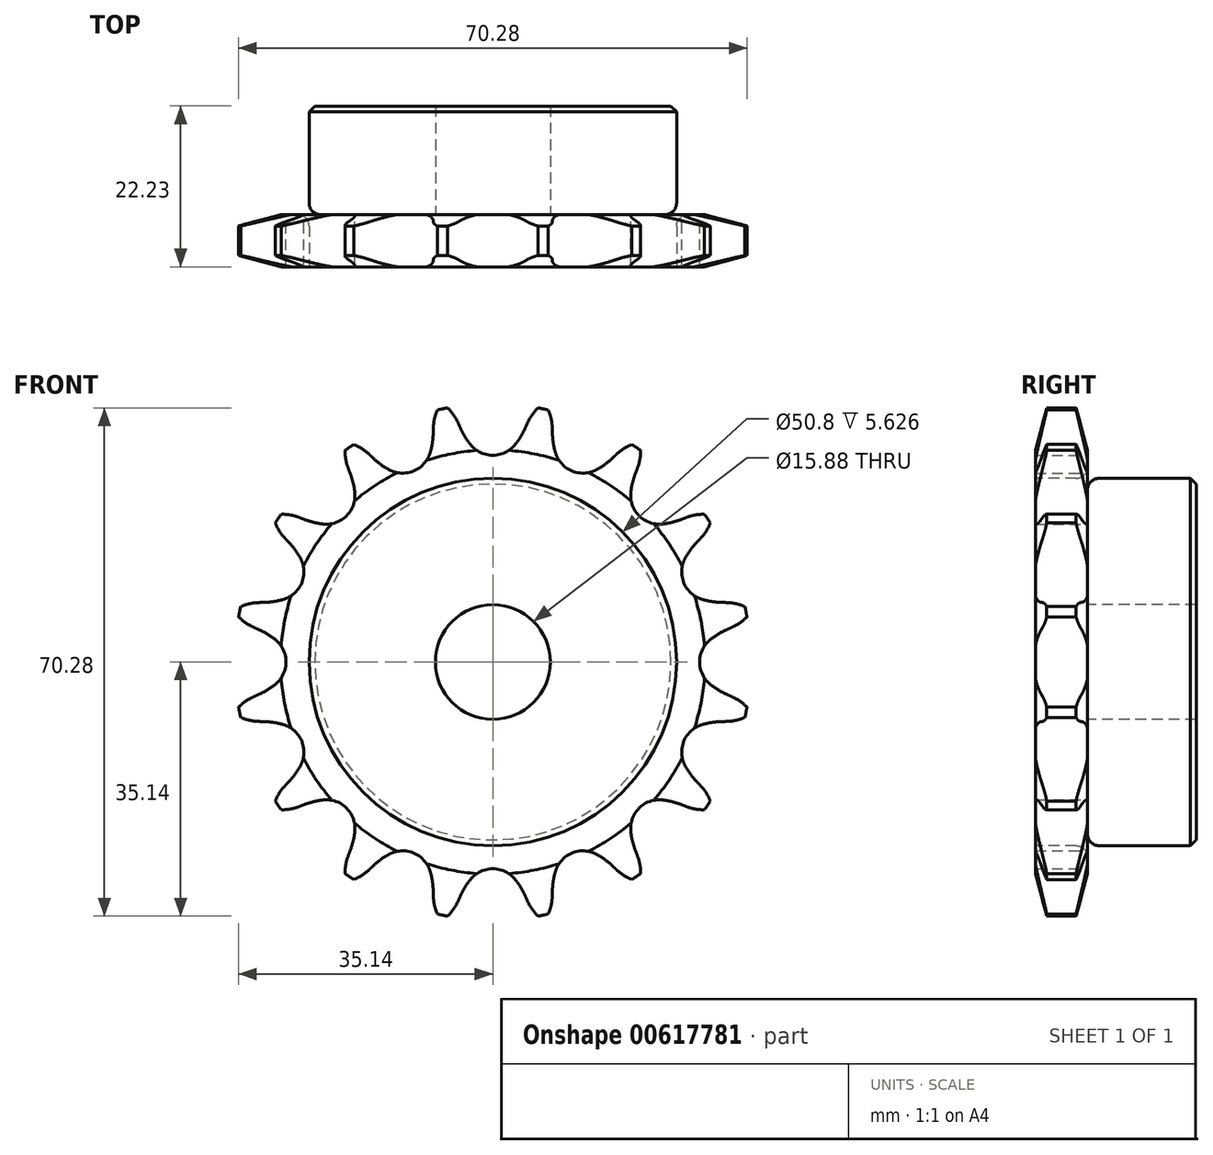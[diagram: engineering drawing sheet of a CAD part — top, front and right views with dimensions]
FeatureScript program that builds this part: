
annotation { "Feature Type Name" : "Feature", "Feature Type Description" : "" }
export const myFeature = defineFeature(function(context is Context, id is Id, definition is map)
    precondition{}
    {
        {
            var Q0;
            Q0=qCreatedBy(makeId("Right.planeOp"),FACE);
            var sketch = newSketch(context, id + "F0", { "sketchPlane" : qUnion([Q0])});
            skLineSegment(sketch, "E0", {"start": v(0, 0) * mm, "end": v(15.45, 0) * mm, "construction": true});
            skLineSegment(sketch, "E1.bottom", {"start": v(0, 7.94) * mm, "end": v(7.21, 7.94) * mm});
            skLineSegment(sketch, "E1.top", {"start": v(0, 35.69) * mm, "end": v(7.21, 35.69) * mm});
            skLineSegment(sketch, "E1.left", {"start": v(0, 7.94) * mm, "end": v(0, 35.69) * mm});
            skLineSegment(sketch, "E1.right", {"start": v(7.21, 7.94) * mm, "end": v(7.21, 35.69) * mm});
            skLineSegment(sketch, "E2.bottom", {"start": v(0, 7.94) * mm, "end": v(22.23, 7.94) * mm});
            skLineSegment(sketch, "E2.top", {"start": v(0, 25.4) * mm, "end": v(22.23, 25.4) * mm});
            skLineSegment(sketch, "E2.left", {"start": v(0, 7.94) * mm, "end": v(0, 25.4) * mm});
            skLineSegment(sketch, "E2.right", {"start": v(22.23, 7.94) * mm, "end": v(22.23, 25.4) * mm});
            skLineSegment(sketch, "E3.MirrorCS", {"start": v(0, -7.94) * mm, "end": v(7.21, -7.94) * mm});
            skLineSegment(sketch, "E4.MirrorCS", {"start": v(22.23, -7.94) * mm, "end": v(22.23, -25.4) * mm});
            skLineSegment(sketch, "E5.MirrorCS", {"start": v(0, -7.94) * mm, "end": v(0, -25.4) * mm});
            skLineSegment(sketch, "E6.MirrorCS", {"start": v(0, -35.69) * mm, "end": v(7.21, -35.69) * mm});
            skLineSegment(sketch, "E7.MirrorCS", {"start": v(0, -7.94) * mm, "end": v(0, -35.69) * mm});
            skLineSegment(sketch, "E8.MirrorCS", {"start": v(7.21, -7.94) * mm, "end": v(7.21, -35.69) * mm});
            skLineSegment(sketch, "E9.MirrorCS", {"start": v(0, -7.94) * mm, "end": v(22.23, -7.94) * mm});
            skLineSegment(sketch, "E10.MirrorCS", {"start": v(0, -25.4) * mm, "end": v(22.23, -25.4) * mm});
            skSolve(sketch);
        }
        {
            var Q0;
            {var subQ0=sQuery(id+"F0.wireOp",EDGE,"E1.top");Q0=makeQuery(id+"F0.imprint","IMPRINT",FACE,{"disambiguationData":[TD([[makeQuery(id+"F0.imprint","IMPRINT",EDGE,{"derivedFrom":subQ0}),-1.0]])]});}
            var Q1;
            {var subQ5=sQuery(id+"F0.wireOp",EDGE,"E2.left");Q1=makeQuery(id+"F0.imprint","IMPRINT",FACE,{"disambiguationData":[TD([[makeQuery(id+"F0.imprint","IMPRINT",EDGE,{"derivedFrom":subQ5}),-1.0]])]});}
            var Q2;
            {var subQ5=sQuery(id+"F0.wireOp",EDGE,"E2.right");Q2=makeQuery(id+"F0.imprint","IMPRINT",FACE,{"disambiguationData":[TD([[makeQuery(id+"F0.imprint","IMPRINT",EDGE,{"derivedFrom":subQ5}),1.0]])]});}
            var Q3;
            Q3=sQuery(id+"F0.wireOp",EDGE,"E0");
            revolve(context, id + "F1", {"entities" : qUnion([Q0, Q1, Q2]), "axis" : qUnion([Q3]), "revolveType" : RevolveType.FULL});
        }
        {
            var Q0;
            Q0=makeQuery(id+"F1.opRevolve","SWEPT_EDGE",EDGE,{"disambiguationData":[OSD([sQuery(id+"F0.wireOp",EDGE,"E1.right"),sQuery(id+"F0.wireOp",EDGE,"E2.top")])]});
            fillet(context, id + "F2", {"entities" : qUnion([Q0]), "radius" : 1.59 * mm, "tangentPropagation" : true, "allowEdgeOverflow" : false});
        }
        {
            var Q0;
            Q0=makeQuery(id+"F1.opRevolve","SWEPT_EDGE",EDGE,{"disambiguationData":[OSD([sQuery(id+"F0.wireOp",EDGE,"E2.top"),sQuery(id+"F0.wireOp",EDGE,"E2.right")])]});
            chamfer(context, id + "F3", {"entities" : qUnion([Q0]), "width" : 0.8 * mm, "tangentPropagation" : true});
        }
        {
            var Q0;
            Q0=makeQuery(id+"F1.opRevolve","SWEPT_EDGE",EDGE,{"disambiguationData":[OSD([sQuery(id+"F0.wireOp",EDGE,"E1.top"),sQuery(id+"F0.wireOp",EDGE,"E1.left")])]});
            var Q1;
            Q1=makeQuery(id+"F1.opRevolve","SWEPT_EDGE",EDGE,{"disambiguationData":[OSD([sQuery(id+"F0.wireOp",EDGE,"E1.top"),sQuery(id+"F0.wireOp",EDGE,"E1.right")])]});
            chamfer(context, id + "F4", {"entities" : qUnion([Q0, Q1]), "chamferType" : ChamferType.TWO_OFFSETS, "width1" : 6.35 * mm, "oppositeDirection" : false, "width2" : 1.57 * mm, "tangentPropagation" : true});
        }
        {
            var Q0;
            Q0=makeQuery(id+"F1.opRevolve","SWEPT_FACE",FACE,{"disambiguationData":[OSD([sQuery(id+"F0.wireOp",EDGE,"E1.left"),sQuery(id+"F0.wireOp",EDGE,"E2.left")])]});
            var sketch = newSketch(context, id + "F5", { "sketchPlane" : qUnion([Q0])});
            skCircle(sketch, "E11", {"center": v(0, 0) * mm, "radius": 32.55 * mm, "construction": true});
            skLineSegment(sketch, "E12", {"start": v(0, 0) * mm, "end": v(0, 32.55) * mm, "construction": true});
            skLineSegment(sketch, "E13", {"start": v(0, 32.55) * mm, "end": v(44.62, 32.55) * mm, "construction": true});
            skLineSegment(sketch, "E14", {"start": v(0, 32.55) * mm, "end": v(5, 36.56) * mm, "construction": true});
            skLineSegment(sketch, "E15", {"start": v(5, 36.56) * mm, "end": v(-4.46, 32.3) * mm, "construction": true});
            skLineSegment(sketch, "E16", {"start": v(-4.46, 32.3) * mm, "end": v(-4.82, 33.1) * mm});
            skLineSegment(sketch, "E17", {"start": v(0, 0) * mm, "end": v(-7.13, 35.85) * mm});
            skArc(sketch, "E18", {"start": v(-7.13, 35.85) * mm, "mid": v(-15.87, 26.15) * mm, "end": v(-4.82, 33.1) * mm, "construction": true});
            skArc(sketch, "E19", {"start": v(-4.82, 33.1) * mm, "mid": v(-5.78, 34.63) * mm, "end": v(-7.13, 35.85) * mm});
            skLineSegment(sketch, "E20", {"start": v(-4.82, 33.1) * mm, "end": v(-4.82, 33.1) * mm});
            skLineSegment(sketch, "E21", {"start": v(0.5, 21.28) * mm, "end": v(0.38, 21.56) * mm, "construction": true});
            skArc(sketch, "E22", {"start": v(-4.46, 32.3) * mm, "mid": v(-3.84, 31.14) * mm, "end": v(-3.1, 30.07) * mm});
            skArc(sketch, "E23", {"start": v(-3.1, 30.07) * mm, "mid": v(13.83, 41.97) * mm, "end": v(-4.46, 32.3) * mm, "construction": true});
            skArc(sketch, "E24.MirrorCS", {"start": v(4.82, 33.1) * mm, "mid": v(5.78, 34.63) * mm, "end": v(7.13, 35.85) * mm});
            skLineSegment(sketch, "E25.MirrorCS", {"start": v(4.46, 32.3) * mm, "end": v(4.82, 33.1) * mm});
            skArc(sketch, "E26.MirrorCS", {"start": v(4.46, 32.3) * mm, "mid": v(3.84, 31.14) * mm, "end": v(3.1, 30.07) * mm});
            skArc(sketch, "E27", {"start": v(3.1, 30.07) * mm, "mid": v(0, 36.51) * mm, "end": v(-3.1, 30.07) * mm, "construction": true});
            skArc(sketch, "E28", {"start": v(-3.1, 30.07) * mm, "mid": v(0, 28.59) * mm, "end": v(3.1, 30.07) * mm});
            skArc(sketch, "E29.1.0", {"start": v(-17.12, 28.74) * mm, "mid": v(-18.6, 29.79) * mm, "end": v(-20.3, 30.4) * mm});
            skLineSegment(sketch, "E29.1.1", {"start": v(-16.48, 28.14) * mm, "end": v(-17.12, 28.74) * mm});
            skArc(sketch, "E29.1.2", {"start": v(-16.48, 28.14) * mm, "mid": v(-15.47, 27.3) * mm, "end": v(-14.36, 26.6) * mm});
            skArc(sketch, "E29.1.3", {"start": v(-14.36, 26.6) * mm, "mid": v(-10.94, 26.41) * mm, "end": v(-8.65, 28.96) * mm});
            skArc(sketch, "E29.1.4", {"start": v(-8.24, 31.55) * mm, "mid": v(-8.37, 30.24) * mm, "end": v(-8.65, 28.96) * mm});
            skLineSegment(sketch, "E29.1.5", {"start": v(-8.24, 31.55) * mm, "end": v(-8.22, 32.42) * mm});
            skArc(sketch, "E29.1.6", {"start": v(-8.22, 32.42) * mm, "mid": v(-7.91, 34.21) * mm, "end": v(-7.13, 35.85) * mm});
            skArc(sketch, "E29.2.0", {"start": v(-26.8, 20) * mm, "mid": v(-28.58, 20.4) * mm, "end": v(-30.4, 20.3) * mm});
            skLineSegment(sketch, "E29.2.1", {"start": v(-26, 19.69) * mm, "end": v(-26.8, 20) * mm});
            skArc(sketch, "E29.2.2", {"start": v(-26, 19.69) * mm, "mid": v(-24.74, 19.3) * mm, "end": v(-23.45, 19.08) * mm});
            skArc(sketch, "E29.2.3", {"start": v(-23.45, 19.08) * mm, "mid": v(-20.21, 20.21) * mm, "end": v(-19.08, 23.45) * mm});
            skArc(sketch, "E29.2.4", {"start": v(-19.69, 26) * mm, "mid": v(-19.3, 24.74) * mm, "end": v(-19.08, 23.45) * mm});
            skLineSegment(sketch, "E29.2.5", {"start": v(-19.69, 26) * mm, "end": v(-20, 26.8) * mm});
            skArc(sketch, "E29.2.6", {"start": v(-20, 26.8) * mm, "mid": v(-20.4, 28.58) * mm, "end": v(-20.3, 30.4) * mm});
            skArc(sketch, "E29.3.0", {"start": v(-32.42, 8.22) * mm, "mid": v(-34.21, 7.91) * mm, "end": v(-35.85, 7.13) * mm});
            skLineSegment(sketch, "E29.3.1", {"start": v(-31.55, 8.24) * mm, "end": v(-32.42, 8.22) * mm});
            skArc(sketch, "E29.3.2", {"start": v(-31.55, 8.24) * mm, "mid": v(-30.24, 8.37) * mm, "end": v(-28.96, 8.65) * mm});
            skArc(sketch, "E29.3.3", {"start": v(-28.96, 8.65) * mm, "mid": v(-26.41, 10.94) * mm, "end": v(-26.6, 14.36) * mm});
            skArc(sketch, "E29.3.4", {"start": v(-28.14, 16.48) * mm, "mid": v(-27.3, 15.47) * mm, "end": v(-26.6, 14.36) * mm});
            skLineSegment(sketch, "E29.3.5", {"start": v(-28.14, 16.48) * mm, "end": v(-28.74, 17.12) * mm});
            skArc(sketch, "E29.3.6", {"start": v(-28.74, 17.12) * mm, "mid": v(-29.79, 18.6) * mm, "end": v(-30.4, 20.3) * mm});
            skArc(sketch, "E29.4.0", {"start": v(-33.1, -4.82) * mm, "mid": v(-34.63, -5.78) * mm, "end": v(-35.85, -7.13) * mm});
            skLineSegment(sketch, "E29.4.1", {"start": v(-32.3, -4.46) * mm, "end": v(-33.1, -4.82) * mm});
            skArc(sketch, "E29.4.2", {"start": v(-32.3, -4.46) * mm, "mid": v(-31.14, -3.84) * mm, "end": v(-30.07, -3.1) * mm});
            skArc(sketch, "E29.4.3", {"start": v(-30.07, -3.1) * mm, "mid": v(-28.59, 0) * mm, "end": v(-30.07, 3.1) * mm});
            skArc(sketch, "E29.4.4", {"start": v(-32.3, 4.46) * mm, "mid": v(-31.14, 3.84) * mm, "end": v(-30.07, 3.1) * mm});
            skLineSegment(sketch, "E29.4.5", {"start": v(-32.3, 4.46) * mm, "end": v(-33.1, 4.82) * mm});
            skArc(sketch, "E29.4.6", {"start": v(-33.1, 4.82) * mm, "mid": v(-34.63, 5.78) * mm, "end": v(-35.85, 7.13) * mm});
            skArc(sketch, "E29.5.0", {"start": v(-28.74, -17.12) * mm, "mid": v(-29.79, -18.6) * mm, "end": v(-30.4, -20.3) * mm});
            skLineSegment(sketch, "E29.5.1", {"start": v(-28.14, -16.48) * mm, "end": v(-28.74, -17.12) * mm});
            skArc(sketch, "E29.5.2", {"start": v(-28.14, -16.48) * mm, "mid": v(-27.3, -15.47) * mm, "end": v(-26.6, -14.36) * mm});
            skArc(sketch, "E29.5.3", {"start": v(-26.6, -14.36) * mm, "mid": v(-26.41, -10.94) * mm, "end": v(-28.96, -8.65) * mm});
            skArc(sketch, "E29.5.4", {"start": v(-31.55, -8.24) * mm, "mid": v(-30.24, -8.37) * mm, "end": v(-28.96, -8.65) * mm});
            skLineSegment(sketch, "E29.5.5", {"start": v(-31.55, -8.24) * mm, "end": v(-32.42, -8.22) * mm});
            skArc(sketch, "E29.5.6", {"start": v(-32.42, -8.22) * mm, "mid": v(-34.21, -7.91) * mm, "end": v(-35.85, -7.13) * mm});
            skArc(sketch, "E29.6.0", {"start": v(-20, -26.8) * mm, "mid": v(-20.4, -28.58) * mm, "end": v(-20.3, -30.4) * mm});
            skLineSegment(sketch, "E29.6.1", {"start": v(-19.69, -26) * mm, "end": v(-20, -26.8) * mm});
            skArc(sketch, "E29.6.2", {"start": v(-19.69, -26) * mm, "mid": v(-19.3, -24.74) * mm, "end": v(-19.08, -23.45) * mm});
            skArc(sketch, "E29.6.3", {"start": v(-19.08, -23.45) * mm, "mid": v(-20.21, -20.21) * mm, "end": v(-23.45, -19.08) * mm});
            skArc(sketch, "E29.6.4", {"start": v(-26, -19.69) * mm, "mid": v(-24.74, -19.3) * mm, "end": v(-23.45, -19.08) * mm});
            skLineSegment(sketch, "E29.6.5", {"start": v(-26, -19.69) * mm, "end": v(-26.8, -20) * mm});
            skArc(sketch, "E29.6.6", {"start": v(-26.8, -20) * mm, "mid": v(-28.58, -20.4) * mm, "end": v(-30.4, -20.3) * mm});
            skArc(sketch, "E29.7.0", {"start": v(-8.22, -32.42) * mm, "mid": v(-7.91, -34.21) * mm, "end": v(-7.13, -35.85) * mm});
            skLineSegment(sketch, "E29.7.1", {"start": v(-8.24, -31.55) * mm, "end": v(-8.22, -32.42) * mm});
            skArc(sketch, "E29.7.2", {"start": v(-8.24, -31.55) * mm, "mid": v(-8.37, -30.24) * mm, "end": v(-8.65, -28.96) * mm});
            skArc(sketch, "E29.7.3", {"start": v(-8.65, -28.96) * mm, "mid": v(-10.94, -26.41) * mm, "end": v(-14.36, -26.6) * mm});
            skArc(sketch, "E29.7.4", {"start": v(-16.48, -28.14) * mm, "mid": v(-15.47, -27.3) * mm, "end": v(-14.36, -26.6) * mm});
            skLineSegment(sketch, "E29.7.5", {"start": v(-16.48, -28.14) * mm, "end": v(-17.12, -28.74) * mm});
            skArc(sketch, "E29.7.6", {"start": v(-17.12, -28.74) * mm, "mid": v(-18.6, -29.79) * mm, "end": v(-20.3, -30.4) * mm});
            skArc(sketch, "E29.8.0", {"start": v(4.82, -33.1) * mm, "mid": v(5.78, -34.63) * mm, "end": v(7.13, -35.85) * mm});
            skLineSegment(sketch, "E29.8.1", {"start": v(4.46, -32.3) * mm, "end": v(4.82, -33.1) * mm});
            skArc(sketch, "E29.8.2", {"start": v(4.46, -32.3) * mm, "mid": v(3.84, -31.14) * mm, "end": v(3.1, -30.07) * mm});
            skArc(sketch, "E29.8.3", {"start": v(3.1, -30.07) * mm, "mid": v(0, -28.59) * mm, "end": v(-3.1, -30.07) * mm});
            skArc(sketch, "E29.8.4", {"start": v(-4.46, -32.3) * mm, "mid": v(-3.84, -31.14) * mm, "end": v(-3.1, -30.07) * mm});
            skLineSegment(sketch, "E29.8.5", {"start": v(-4.46, -32.3) * mm, "end": v(-4.82, -33.1) * mm});
            skArc(sketch, "E29.8.6", {"start": v(-4.82, -33.1) * mm, "mid": v(-5.78, -34.63) * mm, "end": v(-7.13, -35.85) * mm});
            skArc(sketch, "E29.9.0", {"start": v(17.12, -28.74) * mm, "mid": v(18.6, -29.79) * mm, "end": v(20.3, -30.4) * mm});
            skLineSegment(sketch, "E29.9.1", {"start": v(16.48, -28.14) * mm, "end": v(17.12, -28.74) * mm});
            skArc(sketch, "E29.9.2", {"start": v(16.48, -28.14) * mm, "mid": v(15.47, -27.3) * mm, "end": v(14.36, -26.6) * mm});
            skArc(sketch, "E29.9.3", {"start": v(14.36, -26.6) * mm, "mid": v(10.94, -26.41) * mm, "end": v(8.65, -28.96) * mm});
            skArc(sketch, "E29.9.4", {"start": v(8.24, -31.55) * mm, "mid": v(8.37, -30.24) * mm, "end": v(8.65, -28.96) * mm});
            skLineSegment(sketch, "E29.9.5", {"start": v(8.24, -31.55) * mm, "end": v(8.22, -32.42) * mm});
            skArc(sketch, "E29.9.6", {"start": v(8.22, -32.42) * mm, "mid": v(7.91, -34.21) * mm, "end": v(7.13, -35.85) * mm});
            skArc(sketch, "E29.10.0", {"start": v(26.8, -20) * mm, "mid": v(28.58, -20.4) * mm, "end": v(30.4, -20.3) * mm});
            skLineSegment(sketch, "E29.10.1", {"start": v(26, -19.69) * mm, "end": v(26.8, -20) * mm});
            skArc(sketch, "E29.10.2", {"start": v(26, -19.69) * mm, "mid": v(24.74, -19.3) * mm, "end": v(23.45, -19.08) * mm});
            skArc(sketch, "E29.10.3", {"start": v(23.45, -19.08) * mm, "mid": v(20.21, -20.21) * mm, "end": v(19.08, -23.45) * mm});
            skArc(sketch, "E29.10.4", {"start": v(19.69, -26) * mm, "mid": v(19.3, -24.74) * mm, "end": v(19.08, -23.45) * mm});
            skLineSegment(sketch, "E29.10.5", {"start": v(19.69, -26) * mm, "end": v(20, -26.8) * mm});
            skArc(sketch, "E29.10.6", {"start": v(20, -26.8) * mm, "mid": v(20.4, -28.58) * mm, "end": v(20.3, -30.4) * mm});
            skArc(sketch, "E29.11.0", {"start": v(32.42, -8.22) * mm, "mid": v(34.21, -7.91) * mm, "end": v(35.85, -7.13) * mm});
            skLineSegment(sketch, "E29.11.1", {"start": v(31.55, -8.24) * mm, "end": v(32.42, -8.22) * mm});
            skArc(sketch, "E29.11.2", {"start": v(31.55, -8.24) * mm, "mid": v(30.24, -8.37) * mm, "end": v(28.96, -8.65) * mm});
            skArc(sketch, "E29.11.3", {"start": v(28.96, -8.65) * mm, "mid": v(26.41, -10.94) * mm, "end": v(26.6, -14.36) * mm});
            skArc(sketch, "E29.11.4", {"start": v(28.14, -16.48) * mm, "mid": v(27.3, -15.47) * mm, "end": v(26.6, -14.36) * mm});
            skLineSegment(sketch, "E29.11.5", {"start": v(28.14, -16.48) * mm, "end": v(28.74, -17.12) * mm});
            skArc(sketch, "E29.11.6", {"start": v(28.74, -17.12) * mm, "mid": v(29.79, -18.6) * mm, "end": v(30.4, -20.3) * mm});
            skArc(sketch, "E29.12.0", {"start": v(33.1, 4.82) * mm, "mid": v(34.63, 5.78) * mm, "end": v(35.85, 7.13) * mm});
            skLineSegment(sketch, "E29.12.1", {"start": v(32.3, 4.46) * mm, "end": v(33.1, 4.82) * mm});
            skArc(sketch, "E29.12.2", {"start": v(32.3, 4.46) * mm, "mid": v(31.14, 3.84) * mm, "end": v(30.07, 3.1) * mm});
            skArc(sketch, "E29.12.3", {"start": v(30.07, 3.1) * mm, "mid": v(28.59, 0) * mm, "end": v(30.07, -3.1) * mm});
            skArc(sketch, "E29.12.4", {"start": v(32.3, -4.46) * mm, "mid": v(31.14, -3.84) * mm, "end": v(30.07, -3.1) * mm});
            skLineSegment(sketch, "E29.12.5", {"start": v(32.3, -4.46) * mm, "end": v(33.1, -4.82) * mm});
            skArc(sketch, "E29.12.6", {"start": v(33.1, -4.82) * mm, "mid": v(34.63, -5.78) * mm, "end": v(35.85, -7.13) * mm});
            skArc(sketch, "E29.13.0", {"start": v(28.74, 17.12) * mm, "mid": v(29.79, 18.6) * mm, "end": v(30.4, 20.3) * mm});
            skLineSegment(sketch, "E29.13.1", {"start": v(28.14, 16.48) * mm, "end": v(28.74, 17.12) * mm});
            skArc(sketch, "E29.13.2", {"start": v(28.14, 16.48) * mm, "mid": v(27.3, 15.47) * mm, "end": v(26.6, 14.36) * mm});
            skArc(sketch, "E29.13.3", {"start": v(26.6, 14.36) * mm, "mid": v(26.41, 10.94) * mm, "end": v(28.96, 8.65) * mm});
            skArc(sketch, "E29.13.4", {"start": v(31.55, 8.24) * mm, "mid": v(30.24, 8.37) * mm, "end": v(28.96, 8.65) * mm});
            skLineSegment(sketch, "E29.13.5", {"start": v(31.55, 8.24) * mm, "end": v(32.42, 8.22) * mm});
            skArc(sketch, "E29.13.6", {"start": v(32.42, 8.22) * mm, "mid": v(34.21, 7.91) * mm, "end": v(35.85, 7.13) * mm});
            skArc(sketch, "E29.14.0", {"start": v(20, 26.8) * mm, "mid": v(20.4, 28.58) * mm, "end": v(20.3, 30.4) * mm});
            skLineSegment(sketch, "E29.14.1", {"start": v(19.69, 26) * mm, "end": v(20, 26.8) * mm});
            skArc(sketch, "E29.14.2", {"start": v(19.69, 26) * mm, "mid": v(19.3, 24.74) * mm, "end": v(19.08, 23.45) * mm});
            skArc(sketch, "E29.14.3", {"start": v(19.08, 23.45) * mm, "mid": v(20.21, 20.21) * mm, "end": v(23.45, 19.08) * mm});
            skArc(sketch, "E29.14.4", {"start": v(26, 19.69) * mm, "mid": v(24.74, 19.3) * mm, "end": v(23.45, 19.08) * mm});
            skLineSegment(sketch, "E29.14.5", {"start": v(26, 19.69) * mm, "end": v(26.8, 20) * mm});
            skArc(sketch, "E29.14.6", {"start": v(26.8, 20) * mm, "mid": v(28.58, 20.4) * mm, "end": v(30.4, 20.3) * mm});
            skArc(sketch, "E29.15.0", {"start": v(8.22, 32.42) * mm, "mid": v(7.91, 34.21) * mm, "end": v(7.13, 35.85) * mm});
            skLineSegment(sketch, "E29.15.1", {"start": v(8.24, 31.55) * mm, "end": v(8.22, 32.42) * mm});
            skArc(sketch, "E29.15.2", {"start": v(8.24, 31.55) * mm, "mid": v(8.37, 30.24) * mm, "end": v(8.65, 28.96) * mm});
            skArc(sketch, "E29.15.3", {"start": v(8.65, 28.96) * mm, "mid": v(10.94, 26.41) * mm, "end": v(14.36, 26.6) * mm});
            skArc(sketch, "E29.15.4", {"start": v(16.48, 28.14) * mm, "mid": v(15.47, 27.3) * mm, "end": v(14.36, 26.6) * mm});
            skLineSegment(sketch, "E29.15.5", {"start": v(16.48, 28.14) * mm, "end": v(17.12, 28.74) * mm});
            skArc(sketch, "E29.15.6", {"start": v(17.12, 28.74) * mm, "mid": v(18.6, 29.79) * mm, "end": v(20.3, 30.4) * mm});
            skSolve(sketch);
        }
        {
            var Q0;
            Q0 = qSketchRegion(id + "F5", true);
            extrude(context, id + "F6", {"entities" : qUnion([Q0]), "operationType" : NewBodyOperationType.INTERSECT, "endBound" : BoundingType.THROUGH_ALL, "depth" : 25.4 * mm, "offsetDistance" : 25.4 * mm, "hasSecondDirection" : true, "secondDirectionOppositeDirection" : true, "secondDirectionDepth" : 25.4 * mm});
        }
    });
